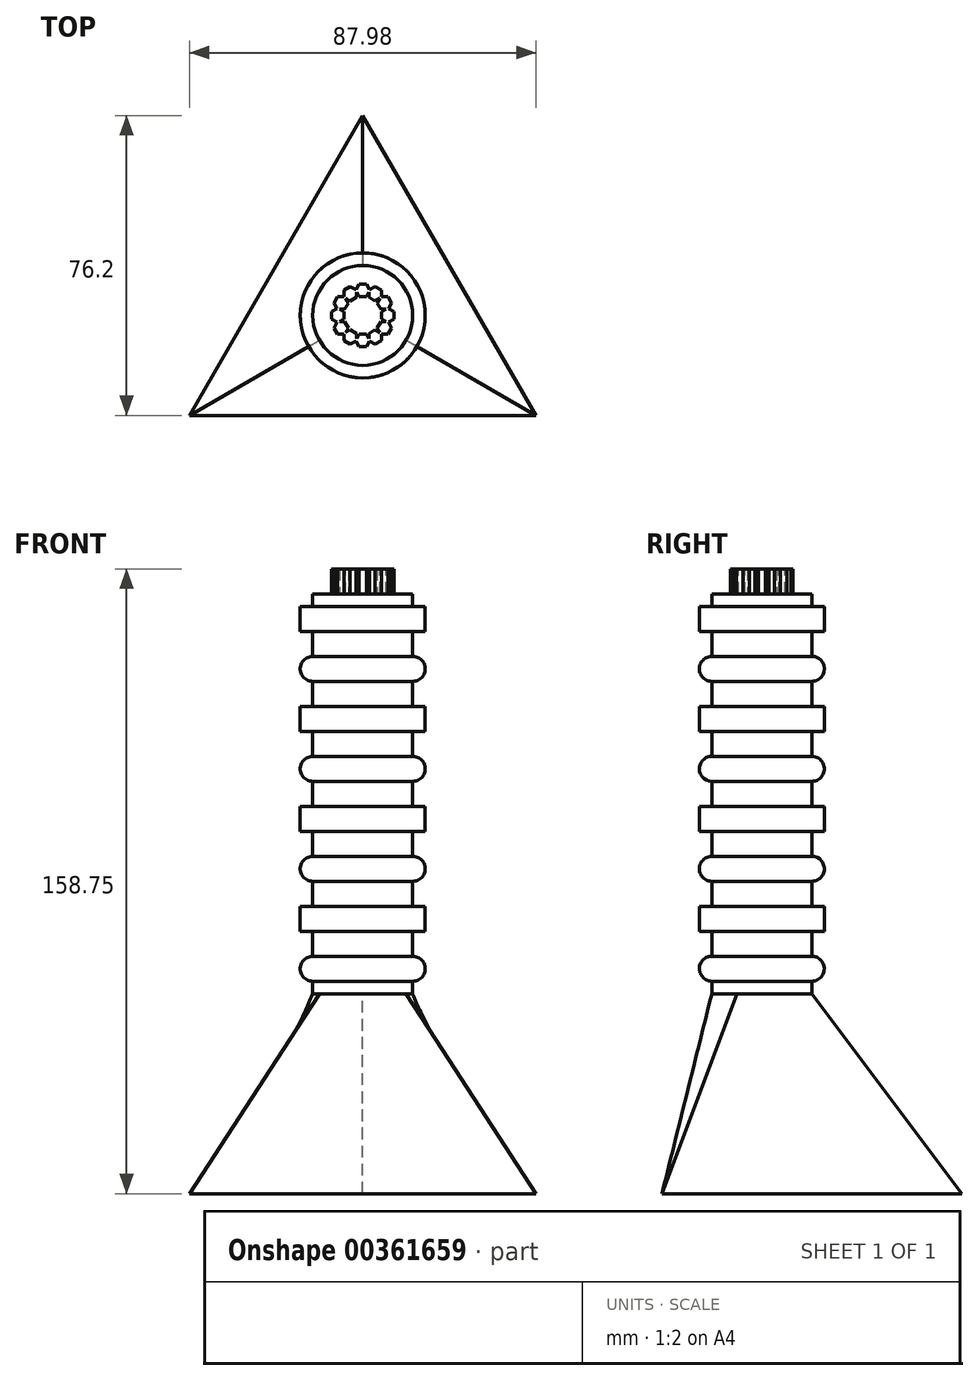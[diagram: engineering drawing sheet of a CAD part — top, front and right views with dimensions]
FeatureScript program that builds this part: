
annotation { "Feature Type Name" : "Feature", "Feature Type Description" : "" }
export const myFeature = defineFeature(function(context is Context, id is Id, definition is map)
    precondition{}
    {
        {
            var Q0;
            Q0=qCreatedBy(makeId("Front.planeOp"),FACE);
            var sketch = newSketch(context, id + "F0", { "sketchPlane" : qUnion([Q0])});
            skPoint(sketch, "E0.middle", {"position": v(0, 0) * mm});
            skLineSegment(sketch, "E1", {"start": v(12.7, 50.8) * mm, "end": v(12.7, 47.62) * mm});
            skLineSegment(sketch, "E2", {"start": v(12.7, 47.62) * mm, "end": v(15.87, 47.62) * mm});
            skLineSegment(sketch, "E3", {"start": v(15.87, 47.62) * mm, "end": v(15.87, 41.27) * mm});
            skLineSegment(sketch, "E4", {"start": v(15.87, 41.27) * mm, "end": v(12.7, 41.27) * mm});
            skLineSegment(sketch, "E5", {"start": v(12.7, 41.27) * mm, "end": v(12.7, 34.92) * mm});
            skArc(sketch, "E6", {"start": v(12.7, 28.57) * mm, "mid": v(15.88, 31.75) * mm, "end": v(12.7, 34.92) * mm});
            skLineSegment(sketch, "E7", {"start": v(12.7, 28.57) * mm, "end": v(12.7, 25.4) * mm});
            skLineSegment(sketch, "E8", {"start": v(12.7, 47.62) * mm, "end": v(12.7, 41.27) * mm, "construction": true});
            skLineSegment(sketch, "E9", {"start": v(12.7, 34.92) * mm, "end": v(12.7, 28.57) * mm, "construction": true});
            skLineSegment(sketch, "E10.direction2", {"start": v(0, 0) * mm, "end": v(0, 0) * mm});
            skLineSegment(sketch, "E11", {"start": v(12.7, 50.8) * mm, "end": v(0, 50.8) * mm});
            skLineSegment(sketch, "E12", {"start": v(0, 50.8) * mm, "end": v(0, -50.8) * mm});
            skLineSegment(sketch, "E13", {"start": v(0, -50.8) * mm, "end": v(12.7, -50.8) * mm});
            skLineSegment(sketch, "E14.0.1.0", {"start": v(12.7, 25.4) * mm, "end": v(12.7, 22.22) * mm});
            skLineSegment(sketch, "E14.0.1.1", {"start": v(12.7, 22.23) * mm, "end": v(15.87, 22.23) * mm});
            skLineSegment(sketch, "E14.0.1.2", {"start": v(15.87, 22.23) * mm, "end": v(15.87, 15.88) * mm});
            skLineSegment(sketch, "E14.0.1.3", {"start": v(15.87, 15.87) * mm, "end": v(12.7, 15.87) * mm});
            skLineSegment(sketch, "E14.0.1.4", {"start": v(12.7, 15.87) * mm, "end": v(12.7, 9.52) * mm});
            skArc(sketch, "E14.0.1.5", {"start": v(12.7, 3.17) * mm, "mid": v(15.88, 6.35) * mm, "end": v(12.7, 9.52) * mm});
            skLineSegment(sketch, "E14.0.1.6", {"start": v(12.7, 3.17) * mm, "end": v(12.7, 0) * mm});
            skLineSegment(sketch, "E14.0.2.0", {"start": v(12.7, 0) * mm, "end": v(12.7, -3.17) * mm});
            skLineSegment(sketch, "E14.0.2.1", {"start": v(12.7, -3.17) * mm, "end": v(15.87, -3.17) * mm});
            skLineSegment(sketch, "E14.0.2.2", {"start": v(15.87, -3.17) * mm, "end": v(15.87, -9.52) * mm});
            skLineSegment(sketch, "E14.0.2.3", {"start": v(15.87, -9.53) * mm, "end": v(12.7, -9.53) * mm});
            skLineSegment(sketch, "E14.0.2.4", {"start": v(12.7, -9.53) * mm, "end": v(12.7, -15.88) * mm});
            skArc(sketch, "E14.0.2.5", {"start": v(12.7, -22.23) * mm, "mid": v(15.88, -19.05) * mm, "end": v(12.7, -15.88) * mm});
            skLineSegment(sketch, "E14.0.2.6", {"start": v(12.7, -22.23) * mm, "end": v(12.7, -25.4) * mm});
            skLineSegment(sketch, "E14.0.3.0", {"start": v(12.7, -25.4) * mm, "end": v(12.7, -28.57) * mm});
            skLineSegment(sketch, "E14.0.3.1", {"start": v(12.7, -28.57) * mm, "end": v(15.87, -28.57) * mm});
            skLineSegment(sketch, "E14.0.3.2", {"start": v(15.87, -28.57) * mm, "end": v(15.87, -34.92) * mm});
            skLineSegment(sketch, "E14.0.3.3", {"start": v(15.87, -34.93) * mm, "end": v(12.7, -34.93) * mm});
            skLineSegment(sketch, "E14.0.3.4", {"start": v(12.7, -34.92) * mm, "end": v(12.7, -41.28) * mm});
            skArc(sketch, "E14.0.3.5", {"start": v(12.7, -47.63) * mm, "mid": v(15.88, -44.45) * mm, "end": v(12.7, -41.28) * mm});
            skLineSegment(sketch, "E14.0.3.6", {"start": v(12.7, -47.62) * mm, "end": v(12.7, -50.8) * mm});
            skLineSegment(sketch, "E14.direction1", {"start": v(12.7, 25.4) * mm, "end": v(38.1, 25.4) * mm, "construction": true});
            skLineSegment(sketch, "E14.direction2", {"start": v(12.7, 25.4) * mm, "end": v(12.7, 0) * mm, "construction": true});
            skSolve(sketch);
        }
        {
            var Q0;
            Q0=qCreatedBy(makeId("Top.planeOp"),FACE);
            cPlane(context, id + "F1", {"entities" : qUnion([Q0]), "cplaneType" : CPlaneType.OFFSET, "offset" : 101.6 * mm, "oppositeDirection" : true, "width" : 152.4 * mm, "height" : 152.4 * mm});
        }
        {
            var Q0;
            Q0=qCreatedBy(id+"F1.planeOp",FACE);
            var sketch = newSketch(context, id + "F2", { "sketchPlane" : qUnion([Q0])});
            skCircle(sketch, "E15.cCircle", {"center": v(0, 0) * mm, "radius": 25.4 * mm, "construction": true});
            skLineSegment(sketch, "E15.0", {"start": v(44, -25.4) * mm, "end": v(-44, -25.4) * mm});
            skLineSegment(sketch, "E15.1", {"start": v(-44, -25.4) * mm, "end": v(0, 50.8) * mm});
            skLineSegment(sketch, "E15.2", {"start": v(0, 50.8) * mm, "end": v(44, -25.4) * mm});
            skPoint(sketch, "E15.0.midPoint", {"position": v(0, -25.4) * mm});
            skSolve(sketch);
        }
        {
            var Q0;
            Q0=qCreatedBy(makeId("Top.planeOp"),FACE);
            cPlane(context, id + "F3", {"entities" : qUnion([Q0]), "cplaneType" : CPlaneType.OFFSET, "offset" : 50.8 * mm, "width" : 152.4 * mm, "height" : 152.4 * mm});
        }
        {
            var Q0;
            Q0=qCreatedBy(id+"F3.planeOp",FACE);
            var sketch = newSketch(context, id + "F4", { "sketchPlane" : qUnion([Q0])});
            skCircle(sketch, "E16", {"center": v(0, 0) * mm, "radius": 6.35 * mm, "construction": true});
            skCircle(sketch, "E17.cCircle", {"center": v(-6.35, 0) * mm, "radius": 1.59 * mm, "construction": true});
            skLineSegment(sketch, "E17.0", {"start": v(-4.76, 0.92) * mm, "end": v(-4.76, -0.92) * mm});
            skLineSegment(sketch, "E17.1", {"start": v(-4.76, -0.92) * mm, "end": v(-6.35, -1.83) * mm});
            skLineSegment(sketch, "E17.2", {"start": v(-6.35, -1.83) * mm, "end": v(-7.94, -0.92) * mm});
            skLineSegment(sketch, "E17.3", {"start": v(-7.94, -0.92) * mm, "end": v(-7.94, 0.92) * mm});
            skLineSegment(sketch, "E17.4", {"start": v(-7.94, 0.92) * mm, "end": v(-6.35, 1.83) * mm});
            skLineSegment(sketch, "E17.5", {"start": v(-6.35, 1.83) * mm, "end": v(-4.76, 0.92) * mm});
            skPoint(sketch, "E17.0.midPoint", {"position": v(-4.76, 0) * mm});
            skSolve(sketch);
        }
        {
            var Q0;
            Q0=makeQuery(id+"F0.imprint","IMPRINT",FACE,{"disambiguationData":[TD([[makeQuery(id+"F0.imprint","IMPRINT",EDGE,{"derivedFrom":sQuery(id+"F0.wireOp",EDGE,"E1")}),-1.0]])]});
            var Q1;
            Q1=sQuery(id+"F0.wireOp",EDGE,"E12");
            revolve(context, id + "F5", {"entities" : qUnion([Q0]), "axis" : qUnion([Q1]), "revolveType" : RevolveType.FULL});
        }
        {
            var Q0;
            Q0=makeQuery(id+"F2.imprint","IMPRINT",FACE,{"disambiguationData":[TD([[makeQuery(id+"F2.imprint","IMPRINT",EDGE,{"derivedFrom":sQuery(id+"F2.wireOp",EDGE,"E15.0")}),-1.0]])]});
            var Q1;
            Q1=makeQuery(id+"F5.opRevolve","SWEPT_FACE",FACE,{"disambiguationData":[OSD([sQuery(id+"F0.wireOp",EDGE,"E13")])]});
            loft(context, id + "F6", {"operationType" : NewBodyOperationType.ADD, "sheetProfilesArray" : [{ "sheetProfileEntities" : qUnion([Q0]) }, { "sheetProfileEntities" : qUnion([Q1]) }]});
        }
        {
            var Q0;
            Q0 = qSketchRegion(id + "F4", true);
            extrude(context, id + "F7", {"entities" : qUnion([Q0]), "depth" : 6.35 * mm});
        }
        {
            var Q0;
            Q0=makeQuery(id+"F7.opExtrude","SWEPT_BODY",BODY,{"disambiguationData":[OSD([sQuery(id+"F4.wireOp",EDGE,"E17.0"),sQuery(id+"F4.wireOp",EDGE,"E17.1"),sQuery(id+"F4.wireOp",EDGE,"E17.2"),sQuery(id+"F4.wireOp",EDGE,"E17.3"),sQuery(id+"F4.wireOp",EDGE,"E17.4"),sQuery(id+"F4.wireOp",EDGE,"E17.5")])]});
            var Q1;
            Q1=makeQuery(id+"F5.opRevolve","SWEPT_EDGE",EDGE,{"disambiguationData":[OSD([sQuery(id+"F0.wireOp",EDGE,"E2"),sQuery(id+"F0.wireOp",EDGE,"E3")])]});
            circularPattern(context, id + "F8", {"operationType" : NewBodyOperationType.ADD, "entities" : qUnion([Q0]), "axis" : qUnion([Q1]), "angle" : 360 * degree, "instanceCount" : 12, "equalSpace" : true});
        }
    });
